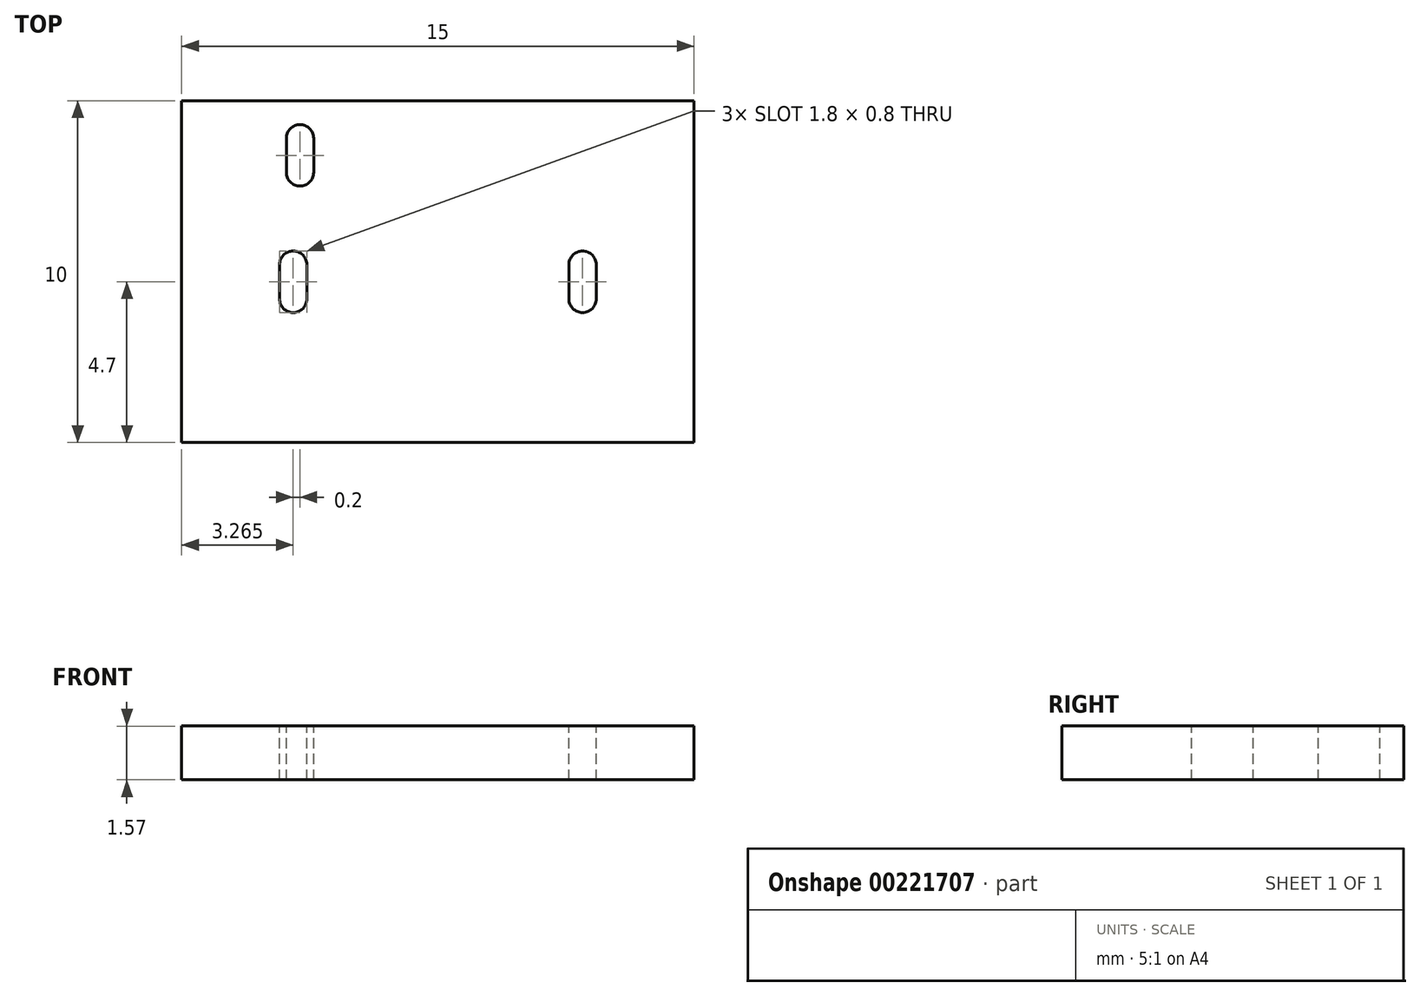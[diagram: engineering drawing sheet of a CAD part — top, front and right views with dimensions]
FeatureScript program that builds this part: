
annotation { "Feature Type Name" : "Feature", "Feature Type Description" : "" }
export const myFeature = defineFeature(function(context is Context, id is Id, definition is map)
    precondition{}
    {
        {
            var Q0;
            Q0=qCreatedBy(makeId("Top.planeOp"),FACE);
            var sketch = newSketch(context, id + "F0", { "sketchPlane" : qUnion([Q0])});
            skLineSegment(sketch, "E0.bottom", {"start": v(-7.5, 0) * mm, "end": v(7.5, 0) * mm});
            skLineSegment(sketch, "E0.top", {"start": v(-7.5, -10) * mm, "end": v(7.5, -10) * mm});
            skLineSegment(sketch, "E0.left", {"start": v(-7.5, 0) * mm, "end": v(-7.5, -10) * mm});
            skLineSegment(sketch, "E0.right", {"start": v(7.5, 0) * mm, "end": v(7.5, -10) * mm});
            skSolve(sketch);
        }
        {
            var Q0;
            Q0 = qSketchRegion(id + "F0", true);
            extrude(context, id + "F1", {"entities" : qUnion([Q0]), "depth" : 1.57 * mm});
        }
        {
            var Q0;
            Q0=makeQuery(id+"F1.opExtrude","CAP_FACE",FACE,{"disambiguationData":[OSD([sQuery(id+"F0.wireOp",EDGE,"E0.bottom"),sQuery(id+"F0.wireOp",EDGE,"E0.top"),sQuery(id+"F0.wireOp",EDGE,"E0.left"),sQuery(id+"F0.wireOp",EDGE,"E0.right")])],"isStart":false});
            var sketch = newSketch(context, id + "F2", { "sketchPlane" : qUnion([Q0])});
            skLineSegment(sketch, "E1", {"start": v(0, 0) * mm, "end": v(0, -10) * mm, "construction": true});
            skLineSegment(sketch, "E2.bottom", {"start": v(-3.64, -2.5) * mm, "end": v(-4.44, -2.5) * mm});
            skLineSegment(sketch, "E2.top", {"start": v(-3.64, -0.7) * mm, "end": v(-4.44, -0.7) * mm});
            skLineSegment(sketch, "E2.left", {"start": v(-3.64, -2.5) * mm, "end": v(-3.64, -0.7) * mm});
            skLineSegment(sketch, "E2.right", {"start": v(-4.44, -2.5) * mm, "end": v(-4.44, -0.7) * mm});
            skPoint(sketch, "E2.middle", {"position": v(-4.04, -1.6) * mm});
            skArc(sketch, "E3", {"start": v(-3.64, -1.1) * mm, "mid": v(-4.04, -0.7) * mm, "end": v(-4.44, -1.1) * mm});
            skArc(sketch, "E4", {"start": v(-4.44, -2.1) * mm, "mid": v(-4.04, -2.5) * mm, "end": v(-3.64, -2.1) * mm});
            skLineSegment(sketch, "E5.bottom", {"start": v(-3.84, -6.2) * mm, "end": v(-4.63, -6.2) * mm});
            skLineSegment(sketch, "E5.top", {"start": v(-3.84, -4.4) * mm, "end": v(-4.63, -4.4) * mm});
            skLineSegment(sketch, "E5.left", {"start": v(-3.84, -6.2) * mm, "end": v(-3.84, -4.4) * mm});
            skLineSegment(sketch, "E5.right", {"start": v(-4.63, -6.2) * mm, "end": v(-4.63, -4.4) * mm});
            skPoint(sketch, "E5.middle", {"position": v(-4.24, -5.3) * mm});
            skArc(sketch, "E6", {"start": v(-3.84, -4.8) * mm, "mid": v(-4.24, -4.4) * mm, "end": v(-4.63, -4.8) * mm});
            skArc(sketch, "E7", {"start": v(-4.63, -5.8) * mm, "mid": v(-4.24, -6.2) * mm, "end": v(-3.83, -5.8) * mm});
            skLineSegment(sketch, "E8.MirrorCS", {"start": v(3.84, -6.2) * mm, "end": v(4.63, -6.2) * mm});
            skLineSegment(sketch, "E9.MirrorCS", {"start": v(3.84, -4.4) * mm, "end": v(4.63, -4.4) * mm});
            skLineSegment(sketch, "E10.MirrorCS", {"start": v(3.84, -6.2) * mm, "end": v(3.84, -4.4) * mm});
            skLineSegment(sketch, "E11.MirrorCS", {"start": v(4.63, -6.2) * mm, "end": v(4.63, -4.4) * mm});
            skArc(sketch, "E12.MirrorCS", {"start": v(4.44, -2.1) * mm, "mid": v(4.04, -2.5) * mm, "end": v(3.64, -2.1) * mm});
            skArc(sketch, "E13.MirrorCS", {"start": v(3.84, -4.8) * mm, "mid": v(4.24, -4.4) * mm, "end": v(4.63, -4.8) * mm});
            skArc(sketch, "E14.MirrorCS", {"start": v(4.63, -5.8) * mm, "mid": v(4.24, -6.2) * mm, "end": v(3.83, -5.8) * mm});
            skArc(sketch, "E15.MirrorCS", {"start": v(3.64, -1.1) * mm, "mid": v(4.04, -0.7) * mm, "end": v(4.44, -1.1) * mm});
            skLineSegment(sketch, "E16.MirrorCS", {"start": v(3.64, -2.5) * mm, "end": v(4.44, -2.5) * mm});
            skLineSegment(sketch, "E17.MirrorCS", {"start": v(3.64, -2.5) * mm, "end": v(3.64, -0.7) * mm});
            skLineSegment(sketch, "E18.MirrorCS", {"start": v(3.64, -0.7) * mm, "end": v(4.44, -0.7) * mm});
            skLineSegment(sketch, "E19.MirrorCS", {"start": v(4.44, -2.5) * mm, "end": v(4.44, -0.7) * mm});
            skPoint(sketch, "E20.MirrorP", {"position": v(4.04, -1.6) * mm});
            skPoint(sketch, "E21.MirrorP", {"position": v(4.24, -5.3) * mm});
            skSolve(sketch);
        }
        {
            var Q0;
            {var subQ0=sQuery(id+"F2.wireOp",EDGE,"E3");var subQ4=sQuery(id+"F2.wireOp",EDGE,"E2.left");var subQ5=makeQuery(id+"F2.imprint","INTERSECT",VERTEX,{"derivedFrom":[subQ4,subQ0]});Q0=makeQuery(id+"F2.imprint","IMPRINT",FACE,{"disambiguationData":[TD([[makeQuery(id+"F2.imprint","IMPRINT",EDGE,{"disambiguationData":[TD([[subQ5,1.0]])],"derivedFrom":subQ4}),1.0]])]});}
            var Q1;
            {var subQ0=sQuery(id+"F2.wireOp",EDGE,"E6");var subQ6=sQuery(id+"F2.wireOp",EDGE,"E5.left");var subQ7=makeQuery(id+"F2.imprint","INTERSECT",VERTEX,{"derivedFrom":[subQ6,subQ0]});Q1=makeQuery(id+"F2.imprint","IMPRINT",FACE,{"disambiguationData":[TD([[makeQuery(id+"F2.imprint","IMPRINT",EDGE,{"disambiguationData":[TD([[subQ7,1.0]])],"derivedFrom":subQ6}),1.0]])]});}
            var Q2;
            {var subQ0=sQuery(id+"F2.wireOp",EDGE,"E13.MirrorCS");var subQ5=sQuery(id+"F2.wireOp",EDGE,"E10.MirrorCS");var subQ9=makeQuery(id+"F2.imprint","INTERSECT",VERTEX,{"derivedFrom":[subQ5,subQ0]});Q2=makeQuery(id+"F2.imprint","IMPRINT",FACE,{"disambiguationData":[TD([[makeQuery(id+"F2.imprint","IMPRINT",EDGE,{"disambiguationData":[TD([[subQ9,1.0]])],"derivedFrom":subQ5}),-1.0]])]});}
            var Q3;
            {var subQ0=sQuery(id+"F2.wireOp",EDGE,"E19.MirrorCS");var subQ5=sQuery(id+"F2.wireOp",EDGE,"E12.MirrorCS");var subQ9=makeQuery(id+"F2.imprint","INTERSECT",VERTEX,{"derivedFrom":[subQ5,subQ0]});Q3=makeQuery(id+"F2.imprint","IMPRINT",FACE,{"disambiguationData":[TD([[makeQuery(id+"F2.imprint","IMPRINT",EDGE,{"disambiguationData":[TD([[subQ9,-1.0]])],"derivedFrom":subQ5}),-1.0]])]});}
            extrude(context, id + "F3", {"entities" : qUnion([Q0, Q1, Q2, Q3]), "operationType" : NewBodyOperationType.REMOVE, "oppositeDirection" : true, "depth" : 25 * mm});
        }
    });
